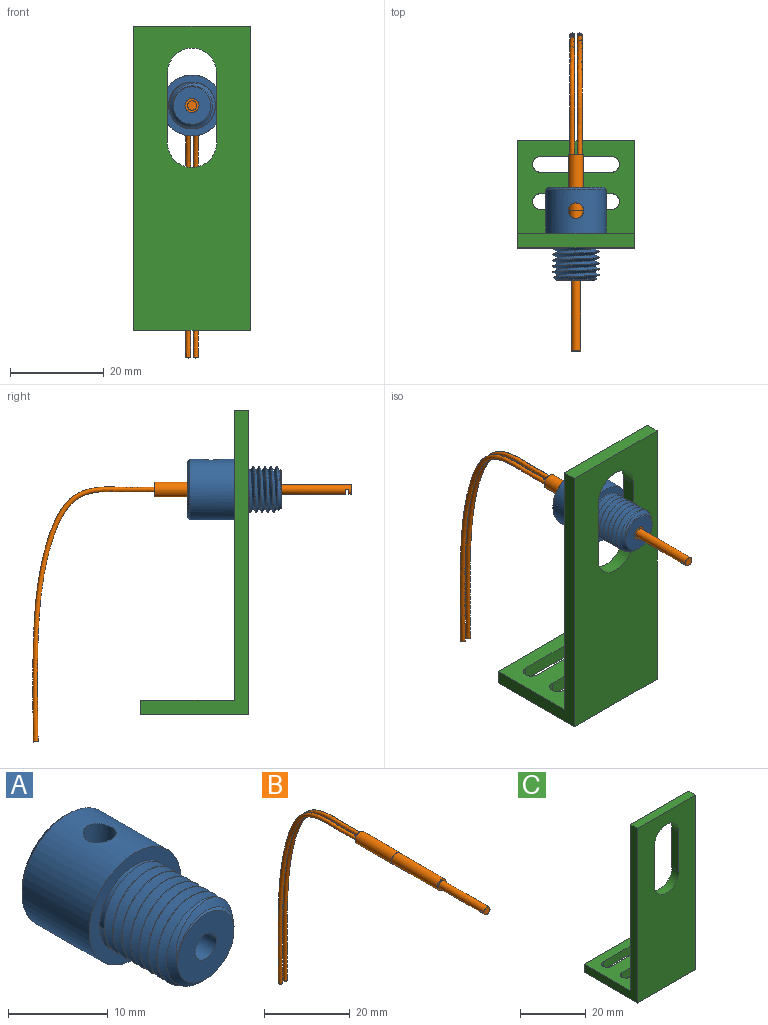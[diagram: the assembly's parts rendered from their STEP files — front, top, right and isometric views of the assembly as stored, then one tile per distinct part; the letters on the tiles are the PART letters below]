
ASSEMBLY  parts=3 mates=2
PART A: 16 faces, bbox 13x20.6x13 mm
  f0: cylinder r=6.5mm len=13mm, axis (0,1,0), area 379.4mm2, adj f3,f12,f15
  f1: cylinder r=1.5mm len=20mm, axis (0,1,0), area 177mm2, adj f2,f4,f12,f13,f14
  f2: plane 8.01x8.01mm, normal (0,-1,0), area 43.2mm2, adj f1,f8,f10,f11
  f3: plane 13x13mm, normal (0,-1,0), area 54.2mm2, adj f0,f5,f6
  f4: plane 12x12mm, normal (0,1,0), area 106mm2, adj f1,f15
  f5: cylinder r=5mm len=10mm, axis (0,1,0), area 3.9mm2, adj f3,f7,f9,f10,f11
  f6: cylinder r=5mm len=9.96mm, axis (0,-1,0), area 4.5mm2, adj f3,f7,f9
  f7: plane 1.2x1.04mm, normal (0,0,-1), area 0.6mm2, adj f5,f6,f9,f10
  f8: plane 0.09x0.05mm, normal (0,0,1), area 0mm2, adj f2,f9,f11
  f9: bspline ~11.55x10.6mm, area 262.8mm2, adj f5,f6,f7,f8,f10,f11
  f10: bspline ~11.55x10.6mm, area 249.4mm2, adj f2,f5,f7,f9,f11
  f11: cone r=4mm half-angle=45deg, axis (0,1,0), area 19.4mm2, adj f2,f5,f8,f9,f10
  f12: cylinder r=1.65mm len=6.5mm, axis (0,0,-1), area 58.2mm2, adj f0,f1,f13,f14
  f13: plane 1.37x0.15mm, normal (0,0,1), area 0.1mm2, adj f1,f12
  f14: plane 1.37x0.15mm, normal (0,0,1), area 0.1mm2, adj f1,f12
  f15: cone r=6.5mm half-angle=45deg, axis (0,-1,0), area 27.8mm2, adj f0,f4
PART B: 14 faces, bbox 3.2x68.6x55.6 mm
  f0: cylinder r=1mm len=15mm, axis (0,1,0), area 91.9mm2, adj f1,f3,f4,f5,f6
  f1: plane 2x2mm, normal (0,-1,0), area 3.1mm2, adj f0
  f2: cylinder r=1.5mm len=15mm, axis (0,-1,0), area 141.4mm2, adj f3,f9
  f3: plane 3x3mm, normal (0,-1,0), area 3.9mm2, adj f0,f2
  f4: plane 2x1mm, normal (0,-1,0), area 1.6mm2, adj f0,f6
  f5: plane 2x1mm, normal (0,1,0), area 1.6mm2, adj f0,f6
  f6: plane 2x0.75mm, normal (0,0,-1), area 1.5mm2, adj f0,f4,f5
  f7: cylinder r=1.6mm len=12mm, axis (0,-1,0), area 120.6mm2, adj f8,f9
  f8: plane 3.2x3.2mm, normal (0,1,0), area 6.5mm2, adj f7,f11,f13
  f9: plane 3.2x3.2mm, normal (0,-1,0), area 1mm2, adj f2,f7
  f10: plane 1x1mm, normal (0,-0.02,-1), area 0.8mm2, adj f11
  f11: bspline ~55.11x26.62mm, area 224.6mm2, adj f8,f10
  f12: plane 1x1mm, normal (0,-0.02,-1), area 0.8mm2, adj f13
  f13: bspline ~55.11x26.62mm, area 224.6mm2, adj f8,f12
PART C: 20 faces, bbox 25x23x65 mm
  f0: plane 25x23mm, normal (0,0,-1), area 450.8mm2, adj f4,f5,f6,f7,f8,f9,f10,f11
  f1: plane 25x20mm, normal (0,0,1), area 375.8mm2, adj f2,f5,f6,f7,f8,f9,f10,f11
  f2: plane 62x25mm, normal (0,1,0), area 1305.9mm2, adj f1,f3,f6,f7,f16,f17,f18,f19
  f3: plane 25x3mm, normal (0,0,1), area 75mm2, adj f2,f4,f6,f7
  f4: plane 65x25mm, normal (0,-1,0), area 1380.9mm2, adj f0,f3,f6,f7,f16,f17,f18,f19
  f5: plane 25x3mm, normal (0,1,0), area 75mm2, adj f0,f1,f6,f7
  f6: plane 65x23mm, normal (1,0,0), area 255mm2, adj f0,f1,f2,f3,f4,f5
  f7: plane 65x23mm, normal (-1,0,0), area 255mm2, adj f0,f1,f2,f3,f4,f5
  f8: plane 15x3mm, normal (0,-1,0), area 45mm2, adj f0,f1,f9,f11
  f9: cylinder r=1.75mm len=3.5mm, axis (0,0,1), area 16.5mm2, adj f0,f1,f8,f10
  f10: plane 15x3mm, normal (0,1,0), area 45mm2, adj f0,f1,f9,f11
  f11: cylinder r=1.75mm len=3.5mm, axis (0,0,1), area 16.5mm2, adj f0,f1,f8,f10
  f12: plane 15x3mm, normal (0,1,0), area 45mm2, adj f0,f1,f13,f15
  f13: cylinder r=1.75mm len=3.5mm, axis (0,0,1), area 16.5mm2, adj f0,f1,f12,f14
  f14: plane 15x3mm, normal (0,-1,0), area 45mm2, adj f0,f1,f13,f15
  f15: cylinder r=1.75mm len=3.5mm, axis (0,0,1), area 16.5mm2, adj f0,f1,f12,f14
  f16: plane 15x3mm, normal (1,0,0), area 45mm2, adj f2,f4,f17,f19
  f17: cylinder r=5.25mm len=10.5mm, axis (0,-1,0), area 49.5mm2, adj f2,f4,f16,f18
  f18: plane 15x3mm, normal (-1,0,0), area 45mm2, adj f2,f4,f17,f19
  f19: cylinder r=5.25mm len=10.5mm, axis (0,-1,0), area 49.5mm2, adj f2,f4,f16,f18
PLACE A t=(1.46,5.18,27.25)mm
PLACE B t=(1.46,-14.82,27.25)mm
PLACE C t=(1.46,-0.67,8.21)mm
MATE fastened A.f0 <-> C.f2  axis (0,-1,0) through (1.46,-4.82,27.25)mm
MATE fastened B.f0 <-> A.f0  axis (0,-1,0) through (1.46,-14.82,27.25)mm
